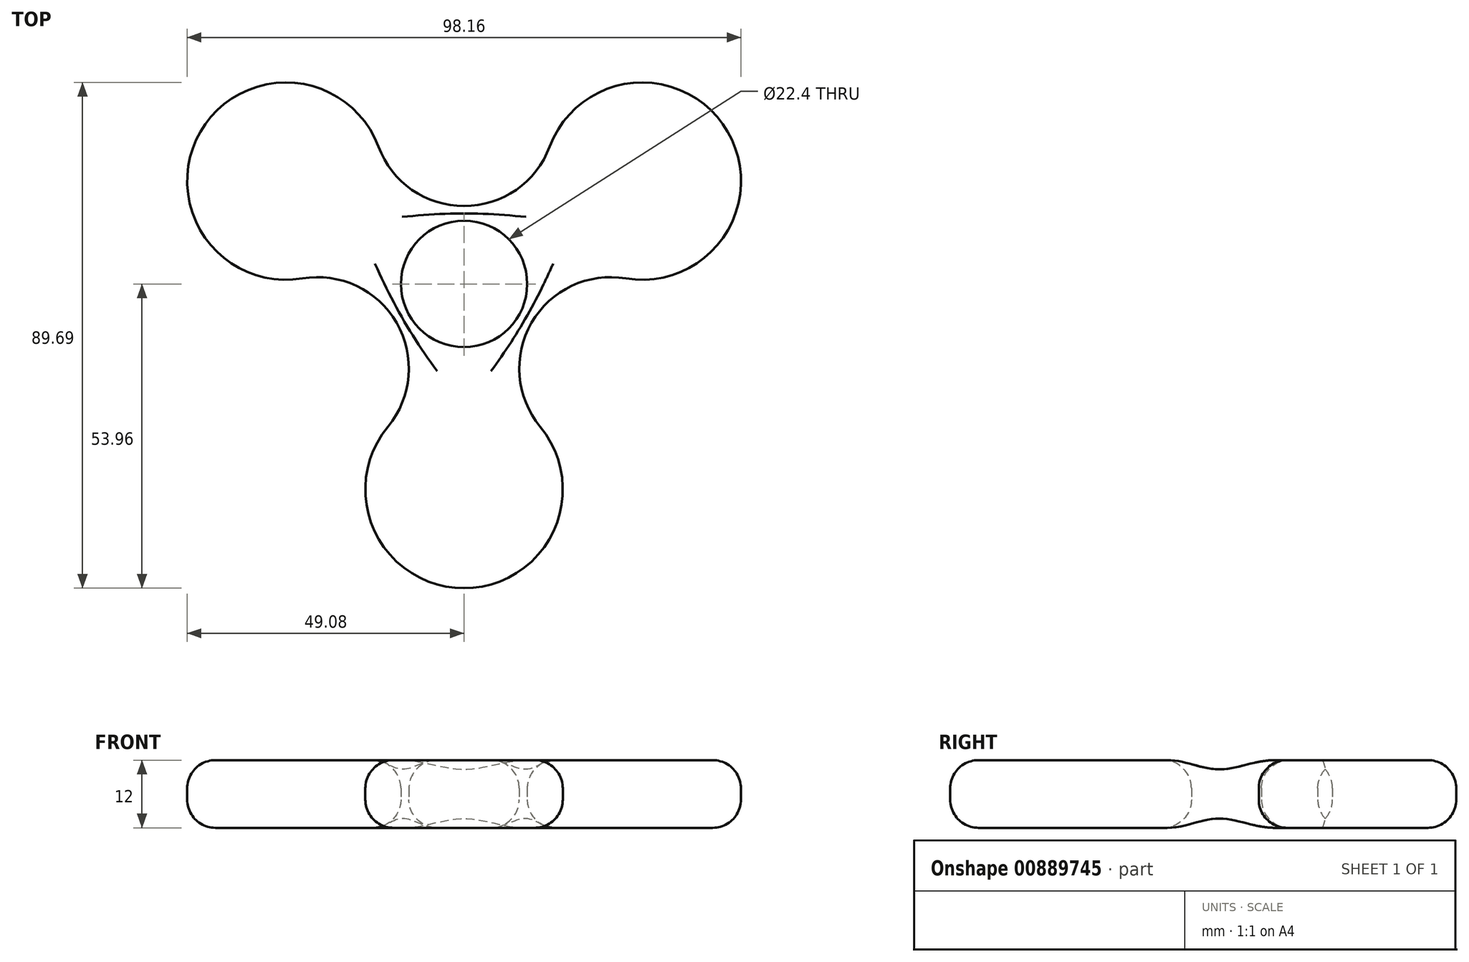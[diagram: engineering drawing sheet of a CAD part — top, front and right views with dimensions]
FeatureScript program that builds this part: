
annotation { "Feature Type Name" : "Feature", "Feature Type Description" : "" }
export const myFeature = defineFeature(function(context is Context, id is Id, definition is map)
    precondition{}
    {
        {
            var Q0;
            Q0=qCreatedBy(makeId("Top.planeOp"),FACE);
            var sketch = newSketch(context, id + "F0", { "sketchPlane" : qUnion([Q0])});
            skCircle(sketch, "E0", {"center": v(0, 0) * mm, "radius": 11.2 * mm});
            skPoint(sketch, "E1.center", {"position": v(0.03, -0.06) * mm});
            skPoint(sketch, "E2.center", {"position": v(0.03, 0) * mm});
            skArc(sketch, "E3", {"start": v(-15.18, 24.34) * mm, "mid": v(0, 13.8) * mm, "end": v(15.18, 24.34) * mm});
            skArc(sketch, "E4", {"start": v(28.67, 0.97) * mm, "mid": v(46.73, 26.98) * mm, "end": v(15.18, 24.34) * mm});
            skArc(sketch, "E5.1.0", {"start": v(-13.5, -25.32) * mm, "mid": v(-11.95, -6.9) * mm, "end": v(-28.67, 0.97) * mm});
            skArc(sketch, "E5.1.1", {"start": v(-15.18, 24.34) * mm, "mid": v(-46.73, 26.98) * mm, "end": v(-28.67, 0.97) * mm});
            skArc(sketch, "E5.2.0", {"start": v(28.67, 0.97) * mm, "mid": v(11.95, -6.9) * mm, "end": v(13.5, -25.32) * mm});
            skArc(sketch, "E5.2.1", {"start": v(-13.5, -25.32) * mm, "mid": v(0, -53.96) * mm, "end": v(13.5, -25.32) * mm});
            skSolve(sketch);
        }
        {
            var Q0;
            Q0=makeQuery(id+"F0.imprint","IMPRINT",FACE,{"disambiguationData":[TD([[makeQuery(id+"F0.imprint","IMPRINT",EDGE,{"derivedFrom":sQuery(id+"F0.wireOp",EDGE,"E0")}),-1.0]])]});
            extrude(context, id + "F1", {"entities" : qUnion([Q0]), "depth" : 12 * mm, "offsetDistance" : 25 * mm});
        }
        {
            var Q0;
            Q0=makeQuery(id+"F1.opExtrude","CAP_FACE",FACE,{"disambiguationData":[OSD([sQuery(id+"F0.wireOp",EDGE,"E0"),sQuery(id+"F0.wireOp",EDGE,"E3"),sQuery(id+"F0.wireOp",EDGE,"E4"),sQuery(id+"F0.wireOp",EDGE,"E5.1.0"),sQuery(id+"F0.wireOp",EDGE,"E5.1.1"),sQuery(id+"F0.wireOp",EDGE,"E5.2.0"),sQuery(id+"F0.wireOp",EDGE,"E5.2.1")])],"isStart":false});
            fillet(context, id + "F2", {"entities" : qUnion([Q0]), "radius" : 5 * mm, "tangentPropagation" : true, "allowEdgeOverflow" : false});
        }
        {
            var Q0;
            Q0=makeQuery(id+"F1.opExtrude","CAP_EDGE",EDGE,{"disambiguationData":[OSD([sQuery(id+"F0.wireOp",EDGE,"E4")])],"isStart":true});
            var Q1;
            Q1=makeQuery(id+"F1.opExtrude","CAP_FACE",FACE,{"disambiguationData":[OSD([sQuery(id+"F0.wireOp",EDGE,"E0"),sQuery(id+"F0.wireOp",EDGE,"E3"),sQuery(id+"F0.wireOp",EDGE,"E4"),sQuery(id+"F0.wireOp",EDGE,"E5.1.0"),sQuery(id+"F0.wireOp",EDGE,"E5.1.1"),sQuery(id+"F0.wireOp",EDGE,"E5.2.0"),sQuery(id+"F0.wireOp",EDGE,"E5.2.1")])],"isStart":true});
            fillet(context, id + "F3", {"entities" : qUnion([Q0, Q1]), "radius" : 5 * mm, "tangentPropagation" : true, "allowEdgeOverflow" : false});
        }
    });
